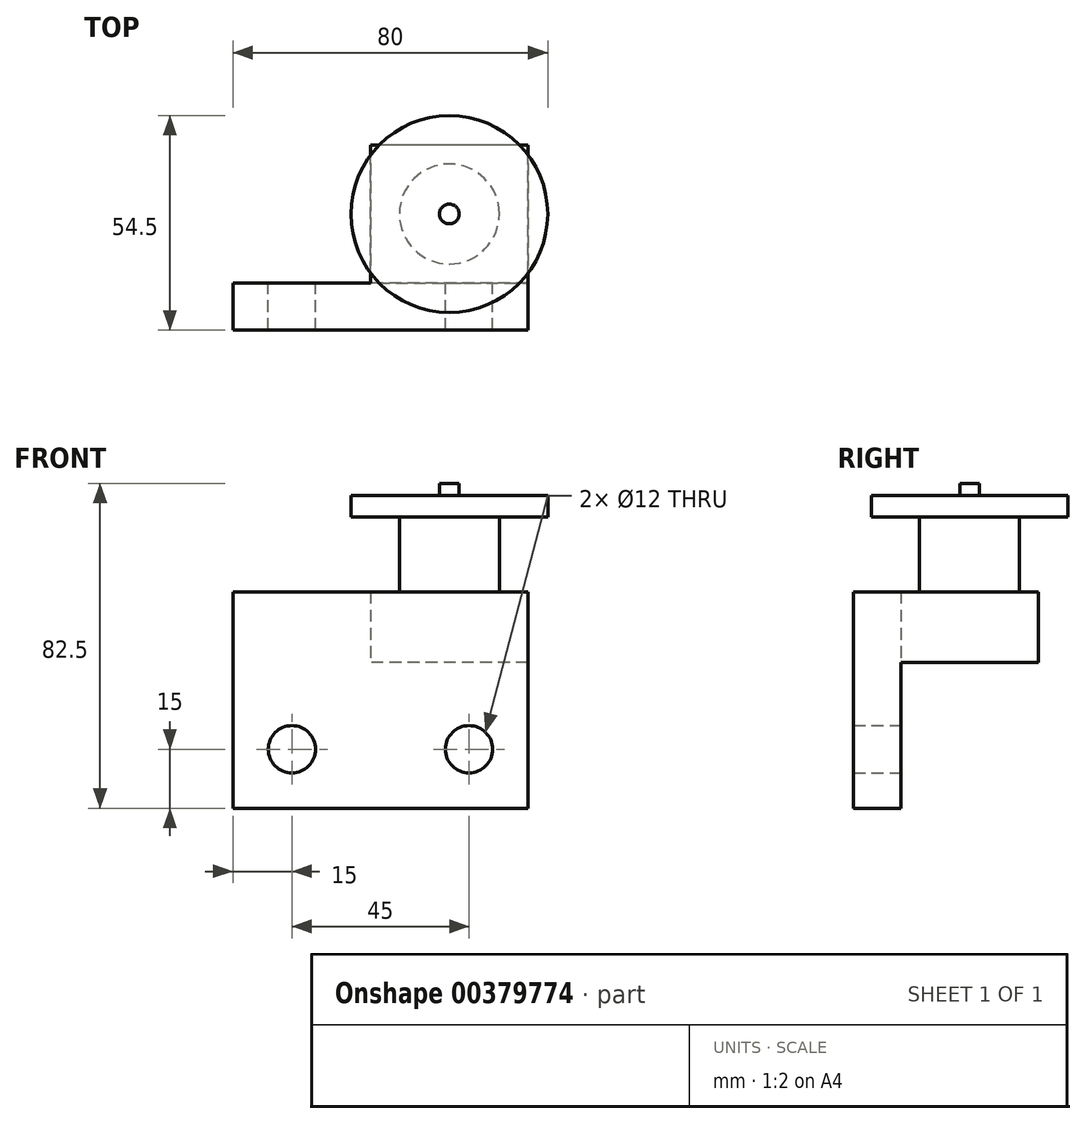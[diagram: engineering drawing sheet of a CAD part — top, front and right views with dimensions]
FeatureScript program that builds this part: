
annotation { "Feature Type Name" : "Feature", "Feature Type Description" : "" }
export const myFeature = defineFeature(function(context is Context, id is Id, definition is map)
    precondition{}
    {
        {
            var Q0;
            Q0=qCreatedBy(makeId("Top.planeOp"),FACE);
            var sketch = newSketch(context, id + "F0", { "sketchPlane" : qUnion([Q0])});
            skLineSegment(sketch, "E0.bottom", {"start": v(50, -17.5) * mm, "end": v(-50, -17.5) * mm});
            skLineSegment(sketch, "E0.top", {"start": v(50, 17.5) * mm, "end": v(-50, 17.5) * mm});
            skLineSegment(sketch, "E0.left", {"start": v(50, -17.5) * mm, "end": v(50, 17.5) * mm});
            skLineSegment(sketch, "E0.right", {"start": v(-50, -17.5) * mm, "end": v(-50, 17.5) * mm});
            skPoint(sketch, "E0.middle", {"position": v(0, 0) * mm});
            skSolve(sketch);
        }
        {
            var Q0;
            Q0=makeQuery(id+"F0.imprint","IMPRINT",FACE,{"disambiguationData":[TD([[makeQuery(id+"F0.imprint","IMPRINT",EDGE,{"derivedFrom":sQuery(id+"F0.wireOp",EDGE,"E0.bottom")}),-1.0]])]});
            extrude(context, id + "F1", {"entities" : qUnion([Q0]), "depth" : -18 * mm});
        }
        {
            var Q0;
            Q0=makeQuery(id+"F1.opExtrude","CAP_FACE",FACE,{"disambiguationData":[OSD([sQuery(id+"F0.wireOp",EDGE,"E0.bottom"),sQuery(id+"F0.wireOp",EDGE,"E0.top"),sQuery(id+"F0.wireOp",EDGE,"E0.left"),sQuery(id+"F0.wireOp",EDGE,"E0.right")])],"isStart":true});
            var sketch = newSketch(context, id + "F2", { "sketchPlane" : qUnion([Q0])});
            skLineSegment(sketch, "E1", {"start": v(50, 0) * mm, "end": v(38, 0) * mm, "construction": true});
            skLineSegment(sketch, "E2", {"start": v(-50, 0) * mm, "end": v(-38, 0) * mm, "construction": true});
            skCircle(sketch, "E3", {"center": v(38, 0) * mm, "radius": 6 * mm});
            skCircle(sketch, "E4", {"center": v(-38, 0) * mm, "radius": 6 * mm});
            skSolve(sketch);
        }
        {
            var Q0;
            Q0=sQuery(id+"F2.wireOp",VERTEX,"E2.end");
            var Q1;
            Q1=sQuery(id+"F2.wireOp",VERTEX,"E3.center");
            var Q2;
            Q2=makeQuery(id+"F1.opExtrude","SWEPT_BODY",BODY,{"disambiguationData":[OSD([sQuery(id+"F0.wireOp",EDGE,"E0.bottom"),sQuery(id+"F0.wireOp",EDGE,"E0.top"),sQuery(id+"F0.wireOp",EDGE,"E0.left"),sQuery(id+"F0.wireOp",EDGE,"E0.right")])]});
            hole(context, id + "F3", {"style" : HoleStyle.SIMPLE, "endStyle" : HoleEndStyle.THROUGH, "holeDiameter" : 12 * mm, "isTappedThrough" : true, "tappedDepth" : 12 * mm, "tapClearance" : 3, "locations" : qUnion([Q0, Q1]), "scope" : qUnion([Q2])});
        }
        {
            var Q0;
            Q0=makeQuery(id+"F1.opExtrude","CAP_FACE",FACE,{"disambiguationData":[OSD([sQuery(id+"F0.wireOp",EDGE,"E0.bottom"),sQuery(id+"F0.wireOp",EDGE,"E0.top"),sQuery(id+"F0.wireOp",EDGE,"E0.left"),sQuery(id+"F0.wireOp",EDGE,"E0.right")])],"isStart":true});
            var sketch = newSketch(context, id + "F4", { "sketchPlane" : qUnion([Q0])});
            skCircle(sketch, "E5", {"center": v(0, 0) * mm, "radius": 12.7 * mm});
            skSolve(sketch);
        }
        {
            var Q0;
            Q0=makeQuery(id+"F4.imprint","IMPRINT",FACE,{"disambiguationData":[TD([[makeQuery(id+"F4.imprint","IMPRINT",EDGE,{"derivedFrom":sQuery(id+"F4.wireOp",EDGE,"E5")}),1.0]])]});
            extrude(context, id + "F5", {"entities" : qUnion([Q0]), "operationType" : NewBodyOperationType.ADD, "depth" : 19 * mm});
        }
        {
            var Q0;
            Q0=makeQuery(id+"F5.opExtrude","CAP_FACE",FACE,{"disambiguationData":[OSD([sQuery(id+"F4.wireOp",EDGE,"E5")])],"isStart":false});
            var sketch = newSketch(context, id + "F6", { "sketchPlane" : qUnion([Q0])});
            skCircle(sketch, "E6", {"center": v(0, 0) * mm, "radius": 25 * mm});
            skSolve(sketch);
        }
        {
            var Q0;
            Q0=makeQuery(id+"F6.imprint","IMPRINT",FACE,{"disambiguationData":[TD([[makeQuery(id+"F6.imprint","IMPRINT",EDGE,{"derivedFrom":sQuery(id+"F6.wireOp",EDGE,"E6")}),1.0]])]});
            var Q1;
            Q1=makeQuery(id+"F6.imprint","IMPRINT",FACE,{"disambiguationData":[TD([[makeQuery(id+"F6.imprint","IMPRINT",EDGE,{"derivedFrom":makeQuery(id+"F5.opExtrude","CAP_EDGE",EDGE,{"disambiguationData":[OSD([sQuery(id+"F4.wireOp",EDGE,"E5")])],"isStart":false})}),1.0]])]});
            extrude(context, id + "F7", {"entities" : qUnion([Q0, Q1]), "operationType" : NewBodyOperationType.ADD, "depth" : 5.5 * mm});
        }
        {
            var Q0;
            Q0=makeQuery(id+"F7.opExtrude","CAP_FACE",FACE,{"disambiguationData":[OSD([sQuery(id+"F6.wireOp",EDGE,"E6")])],"isStart":false});
            var sketch = newSketch(context, id + "F8", { "sketchPlane" : qUnion([Q0])});
            skCircle(sketch, "E7", {"center": v(0, 0) * mm, "radius": 2.5 * mm});
            skSolve(sketch);
        }
        {
            var Q0;
            Q0=qSketchRegion(id+"F8",true);
            extrude(context, id + "F9", {"entities" : qUnion([Q0]), "operationType" : NewBodyOperationType.ADD, "depth" : 3 * mm});
        }
        {
            var Q0;
            Q0=makeQuery(id+"F1.opExtrude","SWEPT_FACE",FACE,{"disambiguationData":[OSD([sQuery(id+"F0.wireOp",EDGE,"E0.bottom")])]});
            var sketch = newSketch(context, id + "F10", { "sketchPlane" : qUnion([Q0])});
            skLineSegment(sketch, "E8.bottom", {"start": v(-50, 0) * mm, "end": v(50, 0) * mm});
            skLineSegment(sketch, "E8.top", {"start": v(-50, -75) * mm, "end": v(50, -75) * mm});
            skLineSegment(sketch, "E8.left", {"start": v(-50, 0) * mm, "end": v(-50, -75) * mm});
            skLineSegment(sketch, "E8.right", {"start": v(50, 0) * mm, "end": v(50, -75) * mm});
            skSolve(sketch);
        }
        {
            var Q0;
            {var subQ0=sQuery(id+"F10.wireOp",EDGE,"E8.top");Q0=makeQuery(id+"F10.imprint","IMPRINT",FACE,{"disambiguationData":[TD([[makeQuery(id+"F10.imprint","IMPRINT",EDGE,{"derivedFrom":subQ0}),1.0]])]});}
            var Q1;
            {var subQ0=sQuery(id+"F10.wireOp",EDGE,"E8.bottom");Q1=makeQuery(id+"F10.imprint","IMPRINT",FACE,{"disambiguationData":[TD([[makeQuery(id+"F10.imprint","IMPRINT",EDGE,{"derivedFrom":subQ0}),1.0]])]});}
            extrude(context, id + "F11", {"entities" : qUnion([Q0, Q1]), "operationType" : NewBodyOperationType.ADD, "depth" : 12 * mm});
        }
        {
            var Q0;
            Q0=makeQuery(id+"F1.opExtrude","CAP_FACE",FACE,{"disambiguationData":[OSD([sQuery(id+"F0.wireOp",EDGE,"E0.bottom"),sQuery(id+"F0.wireOp",EDGE,"E0.top"),sQuery(id+"F0.wireOp",EDGE,"E0.left"),sQuery(id+"F0.wireOp",EDGE,"E0.right")])],"isStart":false});
            var sketch = newSketch(context, id + "F12", { "sketchPlane" : qUnion([Q0])});
            skLineSegment(sketch, "E9", {"start": v(50, -17.5) * mm, "end": v(20, -17.5) * mm});
            skLineSegment(sketch, "E10", {"start": v(20, -17.5) * mm, "end": v(20, 17.5) * mm});
            skLineSegment(sketch, "E11", {"start": v(20, 17.5) * mm, "end": v(50, 17.5) * mm});
            skLineSegment(sketch, "E12", {"start": v(50, 17.5) * mm, "end": v(50, -17.5) * mm});
            skLineSegment(sketch, "E13", {"start": v(0, 17.5) * mm, "end": v(0, -17.5) * mm, "construction": true});
            skLineSegment(sketch, "E14.MirrorCS", {"start": v(-20, -17.5) * mm, "end": v(-20, 17.5) * mm});
            skLineSegment(sketch, "E15.MirrorCS", {"start": v(-50, -17.5) * mm, "end": v(-20, -17.5) * mm});
            skLineSegment(sketch, "E16.MirrorCS", {"start": v(-50, 17.5) * mm, "end": v(-50, -17.5) * mm});
            skLineSegment(sketch, "E17.MirrorCS", {"start": v(-20, 17.5) * mm, "end": v(-50, 17.5) * mm});
            skSolve(sketch);
        }
        {
            var Q0;
            Q0 = qSketchRegion(id + "F12", true);
            extrude(context, id + "F13", {"entities" : qUnion([Q0]), "operationType" : NewBodyOperationType.REMOVE, "oppositeDirection" : true, "depth" : 25 * mm});
        }
        {
            var Q0;
            Q0=makeQuery(id+"F13.boolean.opBoolean","MERGE",FACE,{"derivedFrom":[makeQuery(id+"F11.opExtrude","CAP_FACE",FACE,{"disambiguationData":[OSD([sQuery(id+"F10.wireOp",EDGE,"E8.bottom"),sQuery(id+"F10.wireOp",EDGE,"E8.top"),sQuery(id+"F10.wireOp",EDGE,"E8.left"),sQuery(id+"F10.wireOp",EDGE,"E8.right")])],"isStart":true}),makeQuery(id+"F13.opExtrude","SWEPT_FACE",FACE,{"disambiguationData":[OSD([sQuery(id+"F12.wireOp",EDGE,"E11")])]}),makeQuery(id+"F13.opExtrude","SWEPT_FACE",FACE,{"disambiguationData":[OSD([sQuery(id+"F12.wireOp",EDGE,"E17.MirrorCS")])]})]});
            var sketch = newSketch(context, id + "F14", { "sketchPlane" : qUnion([Q0])});
            skLineSegment(sketch, "E18", {"start": v(-50, 0) * mm, "end": v(-50, -75) * mm});
            skLineSegment(sketch, "E19", {"start": v(-50, -75) * mm, "end": v(-20, -75) * mm});
            skPoint(sketch, "E19.endSnap0", {"position": v(-20, -9) * mm});
            skLineSegment(sketch, "E20", {"start": v(-20, -75) * mm, "end": v(-20, 0) * mm});
            skLineSegment(sketch, "E21", {"start": v(-20, 0) * mm, "end": v(-50, 0) * mm});
            skLineSegment(sketch, "E22", {"start": v(20, 0) * mm, "end": v(20, -75) * mm});
            skLineSegment(sketch, "E23", {"start": v(20, -75) * mm, "end": v(50, -75) * mm});
            skLineSegment(sketch, "E24", {"start": v(50, -75) * mm, "end": v(50, 0) * mm});
            skLineSegment(sketch, "E25", {"start": v(50, 0) * mm, "end": v(20, 0) * mm});
            skSolve(sketch);
        }
        {
            var Q0;
            Q0 = qSketchRegion(id + "F14", true);
            extrude(context, id + "F15", {"entities" : qUnion([Q0]), "operationType" : NewBodyOperationType.REMOVE, "oppositeDirection" : true, "depth" : 25 * mm});
        }
        {
            var Q0;
            Q0=makeQuery(id+"F11.opExtrude","CAP_FACE",FACE,{"disambiguationData":[OSD([sQuery(id+"F10.wireOp",EDGE,"E8.bottom"),sQuery(id+"F10.wireOp",EDGE,"E8.top"),sQuery(id+"F10.wireOp",EDGE,"E8.left"),sQuery(id+"F10.wireOp",EDGE,"E8.right")])],"isStart":false});
            var sketch = newSketch(context, id + "F16", { "sketchPlane" : qUnion([Q0])});
            skLineSegment(sketch, "E26", {"start": v(20, 0) * mm, "end": v(-55, 0) * mm});
            skLineSegment(sketch, "E27", {"start": v(-55, 0) * mm, "end": v(-55, -55) * mm});
            skLineSegment(sketch, "E28", {"start": v(-55, -55) * mm, "end": v(20, -55) * mm});
            skLineSegment(sketch, "E29", {"start": v(20, -55) * mm, "end": v(20, 0) * mm});
            skSolve(sketch);
        }
        {
            var Q0;
            Q0 = qSketchRegion(id + "F16", true);
            extrude(context, id + "F17", {"entities" : qUnion([Q0]), "operationType" : NewBodyOperationType.ADD, "oppositeDirection" : true, "depth" : 12 * mm});
        }
        {
            var Q0;
            Q0=makeQuery(id+"F17.boolean.opBoolean","MERGE",FACE,{"derivedFrom":[makeQuery(id+"F11.opExtrude","CAP_FACE",FACE,{"disambiguationData":[OSD([sQuery(id+"F10.wireOp",EDGE,"E8.bottom"),sQuery(id+"F10.wireOp",EDGE,"E8.top"),sQuery(id+"F10.wireOp",EDGE,"E8.left"),sQuery(id+"F10.wireOp",EDGE,"E8.right")])],"isStart":false}),makeQuery(id+"F17.opExtrude","CAP_FACE",FACE,{"disambiguationData":[OSD([sQuery(id+"F16.wireOp",EDGE,"E26"),sQuery(id+"F16.wireOp",EDGE,"E27"),sQuery(id+"F16.wireOp",EDGE,"E28"),sQuery(id+"F16.wireOp",EDGE,"E29")])],"isStart":true})]});
            var sketch = newSketch(context, id + "F18", { "sketchPlane" : qUnion([Q0])});
            skLineSegment(sketch, "E30", {"start": v(-20, -55) * mm, "end": v(20, -55) * mm});
            skLineSegment(sketch, "E31", {"start": v(20, -55) * mm, "end": v(20, -75) * mm});
            skLineSegment(sketch, "E32", {"start": v(20, -75) * mm, "end": v(-20, -75) * mm});
            skLineSegment(sketch, "E33", {"start": v(-20, -75) * mm, "end": v(-20, -55) * mm});
            skSolve(sketch);
        }
        {
            var Q0;
            Q0 = qSketchRegion(id + "F18", true);
            extrude(context, id + "F19", {"entities" : qUnion([Q0]), "operationType" : NewBodyOperationType.REMOVE, "oppositeDirection" : true, "depth" : 25 * mm});
        }
        {
            var Q0;
            Q0=makeQuery(id+"F17.boolean.opBoolean","MERGE",FACE,{"derivedFrom":[makeQuery(id+"F13.boolean.opBoolean","MERGE",FACE,{"derivedFrom":[makeQuery(id+"F11.opExtrude","CAP_FACE",FACE,{"disambiguationData":[OSD([sQuery(id+"F10.wireOp",EDGE,"E8.bottom"),sQuery(id+"F10.wireOp",EDGE,"E8.top"),sQuery(id+"F10.wireOp",EDGE,"E8.left"),sQuery(id+"F10.wireOp",EDGE,"E8.right")])],"isStart":true}),makeQuery(id+"F13.opExtrude","SWEPT_FACE",FACE,{"disambiguationData":[OSD([sQuery(id+"F12.wireOp",EDGE,"E11")])]}),makeQuery(id+"F13.opExtrude","SWEPT_FACE",FACE,{"disambiguationData":[OSD([sQuery(id+"F12.wireOp",EDGE,"E17.MirrorCS")])]})]}),makeQuery(id+"F17.opExtrude","CAP_FACE",FACE,{"disambiguationData":[OSD([sQuery(id+"F16.wireOp",EDGE,"E26"),sQuery(id+"F16.wireOp",EDGE,"E27"),sQuery(id+"F16.wireOp",EDGE,"E28"),sQuery(id+"F16.wireOp",EDGE,"E29")])],"isStart":false})]});
            var sketch = newSketch(context, id + "F20", { "sketchPlane" : qUnion([Q0])});
            skLineSegment(sketch, "E34", {"start": v(-20, -55) * mm, "end": v(-20, -40) * mm, "construction": true});
            skLineSegment(sketch, "E35", {"start": v(-20, -40) * mm, "end": v(-5, -40) * mm, "construction": true});
            skLineSegment(sketch, "E36", {"start": v(55, -40) * mm, "end": v(40, -40) * mm, "construction": true});
            skSolve(sketch);
        }
        {
            var Q0;
            Q0=sQuery(id+"F20.wireOp",VERTEX,"E35.end");
            var Q1;
            Q1=sQuery(id+"F20.wireOp",VERTEX,"E36.end");
            var Q2;
            Q2=makeQuery(id+"F1.opExtrude","SWEPT_BODY",BODY,{"disambiguationData":[OSD([sQuery(id+"F0.wireOp",EDGE,"E0.bottom"),sQuery(id+"F0.wireOp",EDGE,"E0.top"),sQuery(id+"F0.wireOp",EDGE,"E0.left"),sQuery(id+"F0.wireOp",EDGE,"E0.right")])]});
            hole(context, id + "F21", {"style" : HoleStyle.SIMPLE, "endStyle" : HoleEndStyle.THROUGH, "holeDiameter" : 12 * mm, "isTappedThrough" : true, "tappedDepth" : 12 * mm, "tapClearance" : 3, "locations" : qUnion([Q0, Q1]), "scope" : qUnion([Q2])});
        }
    });
